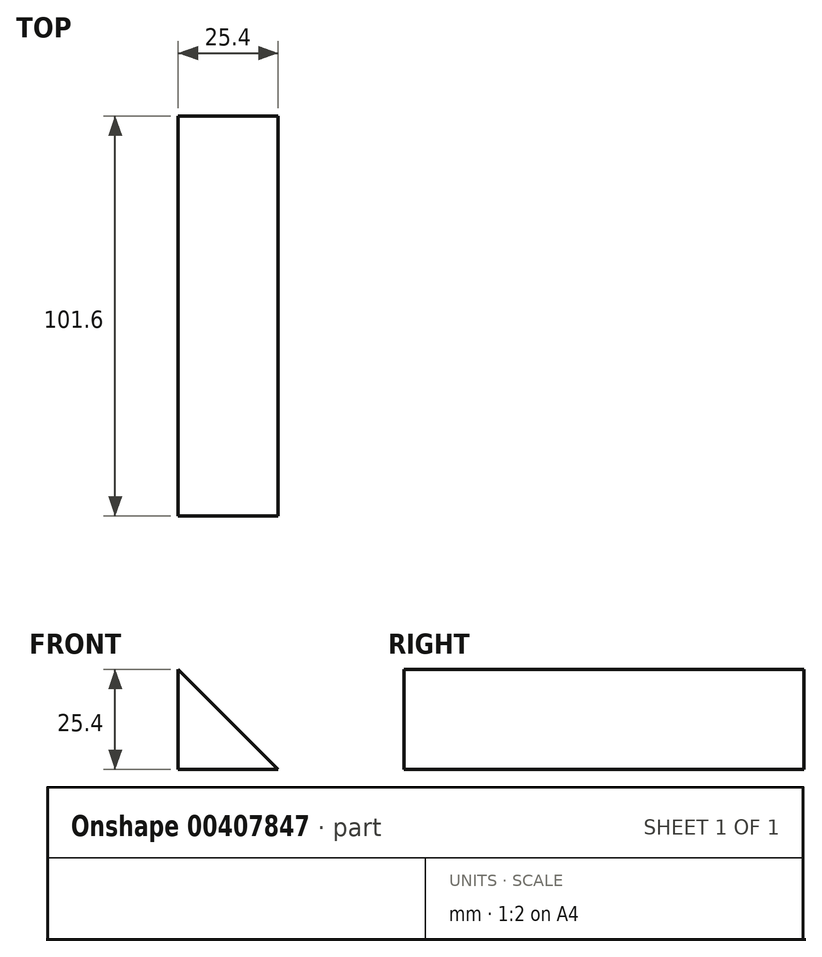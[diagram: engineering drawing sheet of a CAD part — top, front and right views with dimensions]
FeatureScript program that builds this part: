
annotation { "Feature Type Name" : "Feature", "Feature Type Description" : "" }
export const myFeature = defineFeature(function(context is Context, id is Id, definition is map)
    precondition{}
    {
        {
            var Q0;
            Q0=qCreatedBy(makeId("Front.planeOp"),FACE);
            var sketch = newSketch(context, id + "F0", { "sketchPlane" : qUnion([Q0])});
            skLineSegment(sketch, "E0", {"start": v(0, 0) * mm, "end": v(0, 25.4) * mm});
            skLineSegment(sketch, "E1", {"start": v(0, 0) * mm, "end": v(25.4, 0) * mm});
            skLineSegment(sketch, "E2", {"start": v(25.4, 0) * mm, "end": v(0, 25.4) * mm});
            skSolve(sketch);
        }
        {
            var Q0;
            Q0 = qSketchRegion(id + "F0", true);
            extrude(context, id + "F1", {"entities" : qUnion([Q0]), "depth" : 101.6 * mm});
        }
    });
